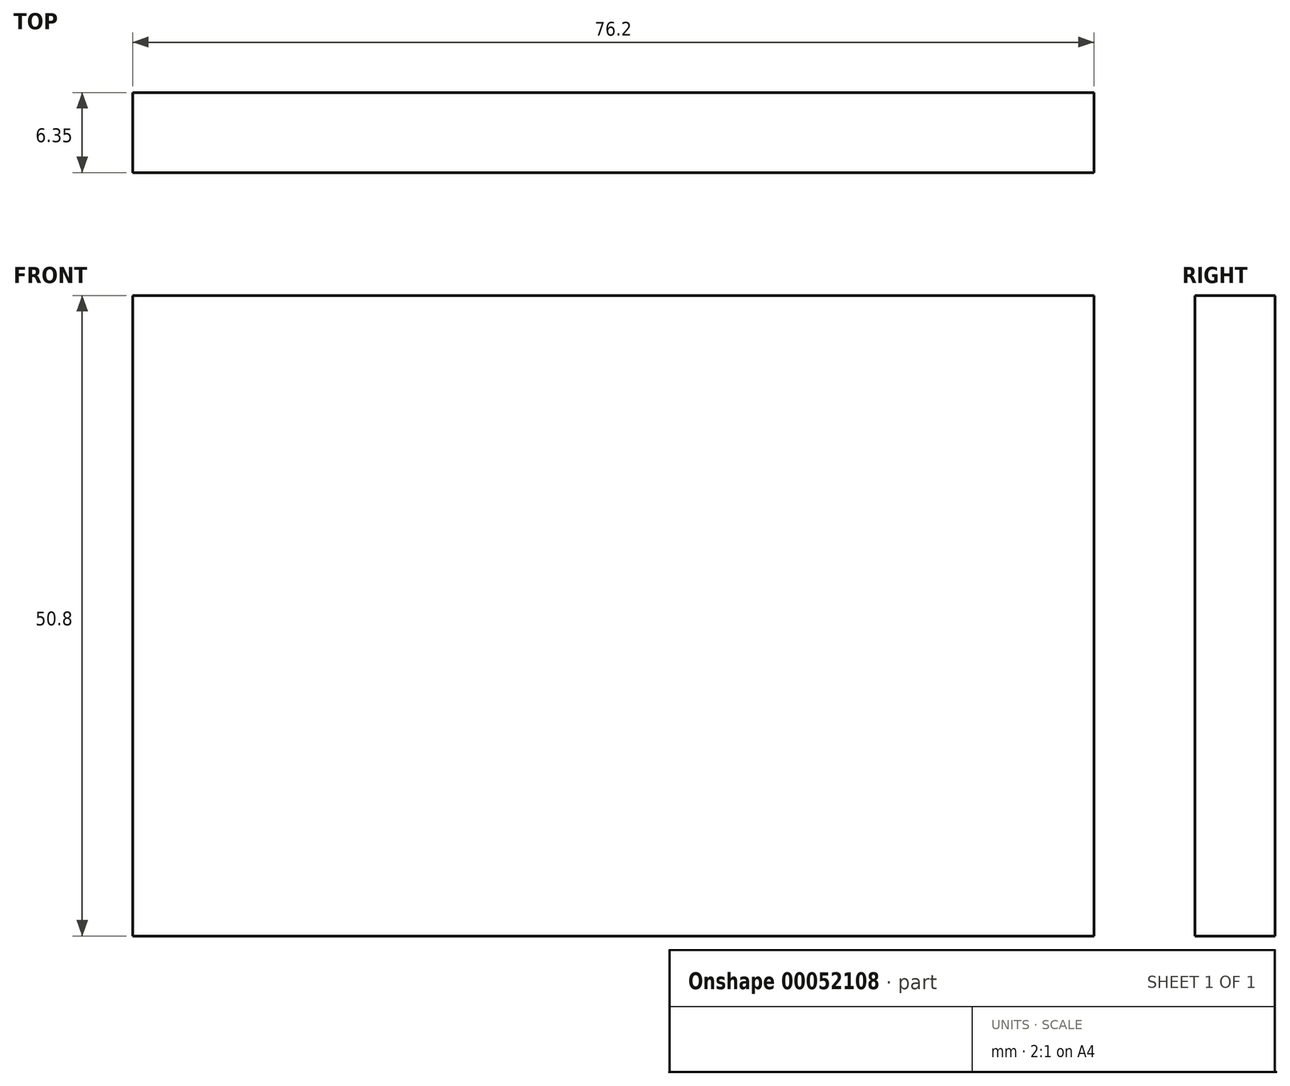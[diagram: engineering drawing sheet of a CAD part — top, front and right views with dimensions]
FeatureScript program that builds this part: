
annotation { "Feature Type Name" : "Feature", "Feature Type Description" : "" }
export const myFeature = defineFeature(function(context is Context, id is Id, definition is map)
    precondition{}
    {
        {
            var Q0;
            Q0=qCreatedBy(makeId("Front.planeOp"),FACE);
            var sketch = newSketch(context, id + "F0", { "sketchPlane" : qUnion([Q0])});
            skLineSegment(sketch, "E0.rect.bottom", {"start": v(-38.1, 25.4) * mm, "end": v(38.1, 25.4) * mm});
            skLineSegment(sketch, "E0.rect.top", {"start": v(-38.1, -25.4) * mm, "end": v(38.1, -25.4) * mm});
            skLineSegment(sketch, "E0.rect.left", {"start": v(-38.1, 25.4) * mm, "end": v(-38.1, -25.4) * mm});
            skLineSegment(sketch, "E0.rect.right", {"start": v(38.1, 25.4) * mm, "end": v(38.1, -25.4) * mm});
            skPoint(sketch, "E0.rect.middle", {"position": v(0, 0) * mm});
            skSolve(sketch);
        }
        {
            var Q0;
            Q0 = qSketchRegion(id + "F0", true);
            extrude(context, id + "F1", {"entities" : qUnion([Q0]), "depth" : 6.35 * mm});
        }
    });
